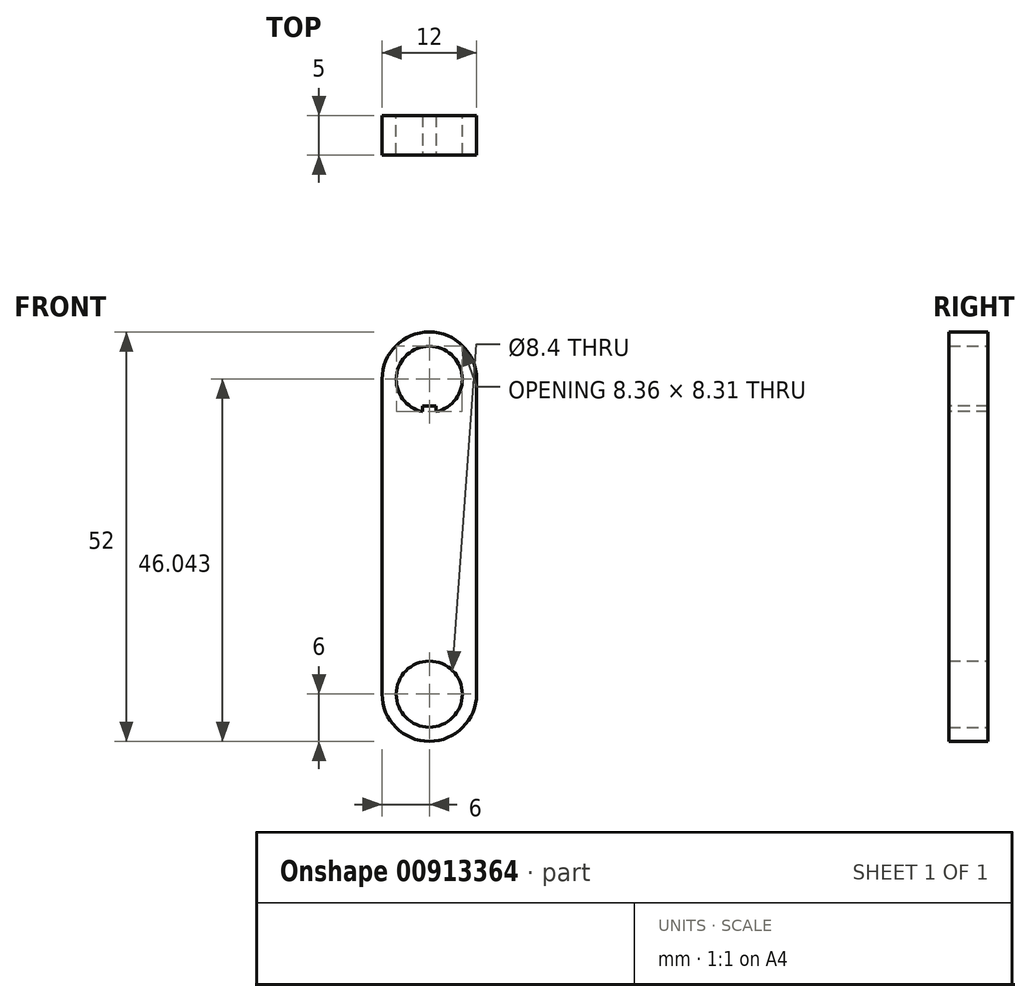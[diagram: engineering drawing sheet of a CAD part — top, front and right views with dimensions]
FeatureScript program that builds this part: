
annotation { "Feature Type Name" : "Feature", "Feature Type Description" : "" }
export const myFeature = defineFeature(function(context is Context, id is Id, definition is map)
    precondition{}
    {
        {
            var Q0;
            Q0=qCreatedBy(makeId("Front.planeOp"),FACE);
            var sketch = newSketch(context, id + "F0", { "sketchPlane" : qUnion([Q0])});
            skArc(sketch, "E0", {"start": v(-6, 0) * mm, "mid": v(0, -6) * mm, "end": v(6, 0) * mm});
            skArc(sketch, "E1", {"start": v(6, 40) * mm, "mid": v(0, 46) * mm, "end": v(-6, 40) * mm});
            skCircle(sketch, "E2", {"center": v(0, 40) * mm, "radius": 4.2 * mm});
            skCircle(sketch, "E3", {"center": v(0, 0) * mm, "radius": 4.2 * mm});
            skLineSegment(sketch, "E4", {"start": v(-6, 0) * mm, "end": v(-6, 40) * mm});
            skLineSegment(sketch, "E5.MirrorCS", {"start": v(6, 0) * mm, "end": v(6, 40) * mm});
            skSolve(sketch);
        }
        {
            var Q0;
            Q0=qSketchRegion(id+"F0",true);
            extrude(context, id + "F1", {"entities" : qUnion([Q0]), "depth" : 5 * mm, "offsetDistance" : 25 * mm});
        }
        {
            var Q0;
            Q0=makeQuery(id+"F1.opExtrude","CAP_FACE",FACE,{"disambiguationData":[OSD([sQuery(id+"F0.wireOp",EDGE,"E0"),sQuery(id+"F0.wireOp",EDGE,"E1"),sQuery(id+"F0.wireOp",EDGE,"E2"),sQuery(id+"F0.wireOp",EDGE,"E3"),sQuery(id+"F0.wireOp",EDGE,"E4"),sQuery(id+"F0.wireOp",EDGE,"E5.MirrorCS")])],"isStart":false});
            var sketch = newSketch(context, id + "F2", { "sketchPlane" : qUnion([Q0])});
            skLineSegment(sketch, "E6", {"start": v(-0.85, 35.89) * mm, "end": v(-0.85, 36.59) * mm});
            skLineSegment(sketch, "E7", {"start": v(-0.85, 36.59) * mm, "end": v(0.85, 36.59) * mm});
            skLineSegment(sketch, "E8", {"start": v(0.85, 36.59) * mm, "end": v(0.85, 35.89) * mm});
            skLineSegment(sketch, "E9", {"start": v(0.85, 35.89) * mm, "end": v(0, 14.84) * mm});
            skLineSegment(sketch, "E10", {"start": v(0, 14.84) * mm, "end": v(-0.85, 35.89) * mm});
            skSolve(sketch);
        }
        {
            var Q0;
            Q0=qSketchRegion(id+"F2",true);
            var Q1;
            Q1=makeQuery(id+"F1.opExtrude","CAP_FACE",FACE,{"disambiguationData":[OSD([sQuery(id+"F0.wireOp",EDGE,"E0"),sQuery(id+"F0.wireOp",EDGE,"E1"),sQuery(id+"F0.wireOp",EDGE,"E2"),sQuery(id+"F0.wireOp",EDGE,"E3"),sQuery(id+"F0.wireOp",EDGE,"E4"),sQuery(id+"F0.wireOp",EDGE,"E5.MirrorCS")])],"isStart":true});
            extrude(context, id + "F3", {"entities" : qUnion([Q0]), "operationType" : NewBodyOperationType.ADD, "endBound" : BoundingType.UP_TO_SURFACE, "oppositeDirection" : true, "depth" : 25 * mm, "endBoundEntityFace" : qUnion([Q1]), "offsetDistance" : 25 * mm});
        }
        {
            var Q0;
            Q0=qCreatedBy(makeId("Top.planeOp"),FACE);
            cPlane(context, id + "F4", {"entities" : qUnion([Q0]), "cplaneType" : CPlaneType.OFFSET, "offset" : 20 * mm, "width" : 150 * mm, "height" : 150 * mm});
        }
    });
